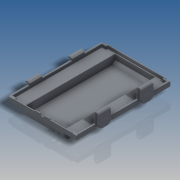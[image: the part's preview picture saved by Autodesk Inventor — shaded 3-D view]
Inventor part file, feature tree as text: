
AUTODESK INVENTOR PART (.ipt)
format: ipt  version: 2016 SP2 (Build 200236200, 236)  size: 802,304 bytes
history: native  units: in
note: dims shown in document units (in); Inventor stores cm internally (conversion verified against a paired STEP export)
features: extrude x14, sketch x6, plane x2, mirror x1, chamfer x1, fillet x1
ambient origin geometry x8: Origin, YZ Plane, XZ Plane, XY Plane, X Axis, Y Axis, Z Axis, Center Point
bodies: Solid1 (feature_tree)
feature tree (25):
  sketch  "Sketch2"  dims[d0=3.4961in d1=2.5197in]
  extrude  "Extrusion1"  Depth=2.5197in
  extrude  "Extrusion2"  Depth=0.0157in
  sketch  "Sketch3"  dims[d2=0.1732in d3=0.0157in]
  extrude  "Extrusion3"  Depth=0.7087in
  extrude  "Extrusion4"  Depth=0.1732in TaperAngle=0.0deg
  plane  "Work Plane1"
  sketch  "Sketch4"  dims[d4=0.7087in d5=0.5039in]
  extrude  "Extrusion5"  Depth=0.1575in
  extrude  "Extrusion6"  Depth=3.4331in
  sketch  "Sketch5"  dims[d6=0.0472in d7=0.1732in d8=0.0in]
  extrude  "Extrusion7"  Depth=0.1102in TaperAngle=0.0deg
  extrude  "Extrusion8"  Depth=0.0315in
  extrude  "Extrusion9"  Depth=0.0315in
  mirror  "Mirror1"
  chamfer  "Chamfer1"  Distance=0.2835in
  sketch  "Sketch6"  dims[d9=2.3937in d10=0.1575in]
  extrude  "Extrusion10"  Depth=0.2992in
  extrude  "Extrusion11"  Depth=3.3701in
  plane  "Work Plane2"
  extrude  "Extrusion14"  Depth=0.189in
  extrude  "Extrusion12"  Depth=0.0315in
  extrude  "Extrusion13"  TaperAngle=0.0deg  [1 undecoded]
  fillet  "Fillet1"  Radius=1.4803in
  sketch  "Sketch7"  dims[d11=0.063in d12=3.4331in d13=0.1102in d14=0.0in d15=3.4646in d16=3.1811in d17=0.2835in d18=0.2992in d19=3.3701in d20=0.189in d21=1.5748in d22=0.0in d23=1.4803in d24=0.0in d25=0.0472in d26=0.3622in d27=0.1575in d28=0.0945in d29=0.4724in d30=0.0in d31=0.0157in d32=0.0472in d33=0.2047in d34=0.0315in d35=0.2205in d36=0.0in d37=0.4409in d38=0.1575in d39=0.2205in d40=0.0in d41=0.2205in d42=0.0in d43=0.0472in d44=0.0472in d45=0.063in d46=0.0787in d47=0.0787in d48=0.4724in d49=0.0in d50=0.0315in d51=0.0787in d52=45.0deg d54=0.189in d55=0.1575in d57=0.0157in d59=0.0315in d60=0.4724in d61=0.0in d62=0.4724in d63=0.0in d64=0.1417in d65=0.126in d66=0.1575in d67=0.2047in d68=0.2047in d69=0.1102in d70=0.3307in d71=0.0in d72=0.126in d73=0.0in d74=0.189in d75=0.2992in d76=0.4567in d77=0.126in d78=0.0in d79=0.0039in d80=0.0315in]
note: 1 required parameter value undecoded (feature->parameter linkage not recoverable at this tier; creation-order binding heuristic only, values carry confidence <= 0.55)
